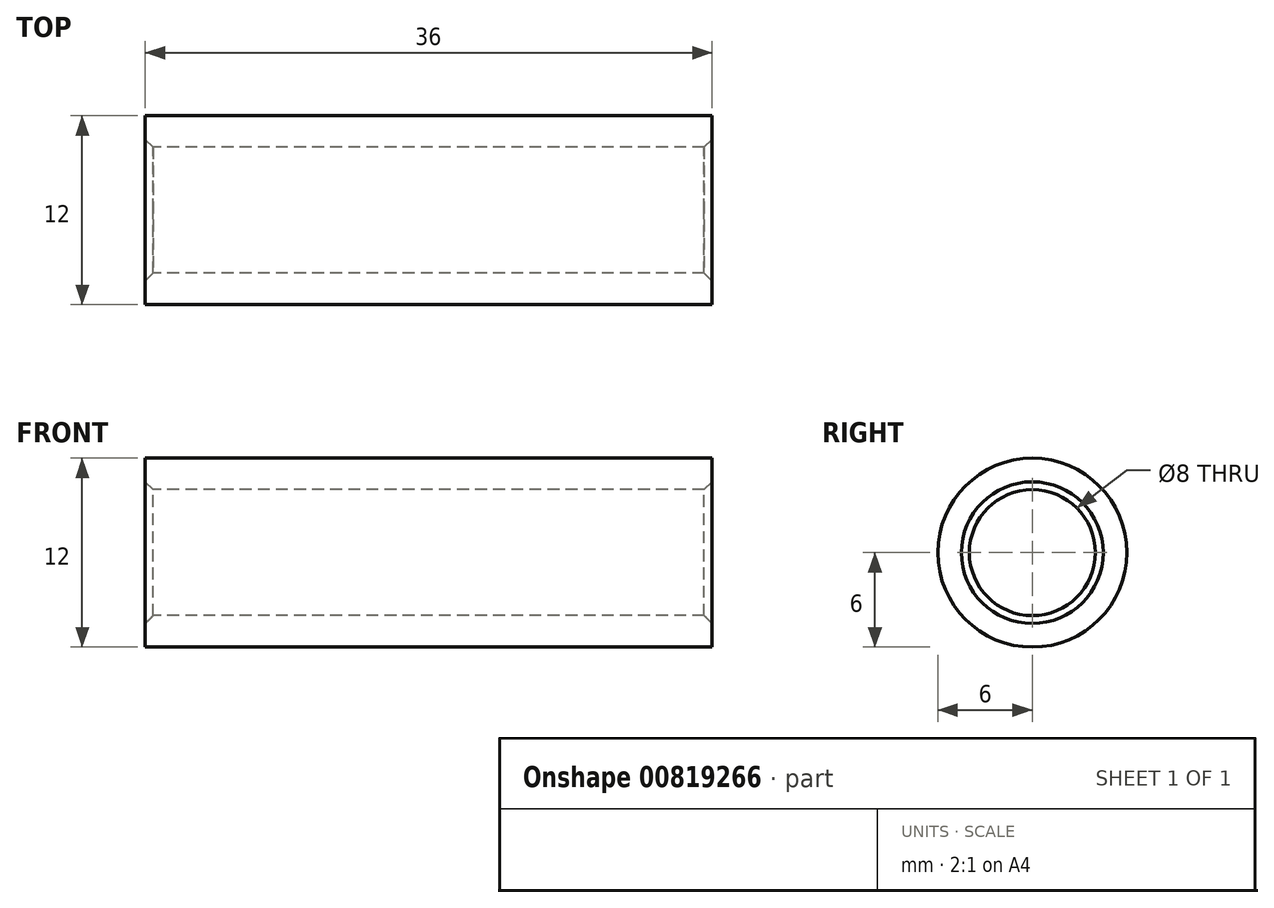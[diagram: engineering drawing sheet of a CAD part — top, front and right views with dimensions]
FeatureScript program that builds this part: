
annotation { "Feature Type Name" : "Feature", "Feature Type Description" : "" }
export const myFeature = defineFeature(function(context is Context, id is Id, definition is map)
    precondition{}
    {
        {
            var Q0;
            Q0=qCreatedBy(makeId("Front.planeOp"),FACE);
            var sketch = newSketch(context, id + "F0", { "sketchPlane" : qUnion([Q0])});
            skLineSegment(sketch, "E0.bottom", {"start": v(-18, 6) * mm, "end": v(18, 6) * mm});
            skLineSegment(sketch, "E0.top", {"start": v(-18, 4) * mm, "end": v(18, 4) * mm});
            skLineSegment(sketch, "E0.left", {"start": v(-18, 6) * mm, "end": v(-18, 4) * mm});
            skLineSegment(sketch, "E0.right", {"start": v(18, 6) * mm, "end": v(18, 4) * mm});
            skLineSegment(sketch, "E1", {"start": v(-16.73, 0) * mm, "end": v(15.24, 0) * mm, "construction": true});
            skSolve(sketch);
        }
        {
            var Q0;
            Q0=makeQuery(id+"F0.imprint","IMPRINT",FACE,{"disambiguationData":[TD([[makeQuery(id+"F0.imprint","IMPRINT",EDGE,{"derivedFrom":sQuery(id+"F0.wireOp",EDGE,"E0.bottom")}),-1.0]])]});
            var Q1;
            Q1=sQuery(id+"F0.wireOp",EDGE,"E1");
            var Q2;
            Q2=sQuery(id+"F0.wireOp",EDGE,"E0.bottom");
            var Q3;
            Q3=sQuery(id+"F0.wireOp",EDGE,"E0.top");
            var Q4;
            Q4=sQuery(id+"F0.wireOp",EDGE,"E1");
            revolve(context, id + "F1", {"surfaceOperationType" : NewSurfaceOperationType.NEW, "entities" : qUnion([Q0]), "surfaceEntities" : qUnion([Q1, Q2, Q3]), "axis" : qUnion([Q4]), "revolveType" : RevolveType.FULL});
        }
        {
            var Q0;
            Q0=makeQuery(id+"F1.opRevolve","SWEPT_EDGE",EDGE,{"disambiguationData":[OSD([sQuery(id+"F0.wireOp",EDGE,"E0.top"),sQuery(id+"F0.wireOp",EDGE,"E0.right")])]});
            var Q1;
            Q1=makeQuery(id+"F1.opRevolve","SWEPT_EDGE",EDGE,{"disambiguationData":[OSD([sQuery(id+"F0.wireOp",EDGE,"E0.top"),sQuery(id+"F0.wireOp",EDGE,"E0.left")])]});
            chamfer(context, id + "F2", {"entities" : qUnion([Q0, Q1]), "width" : 0.5 * mm, "tangentPropagation" : true});
        }
    });
